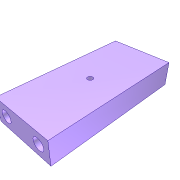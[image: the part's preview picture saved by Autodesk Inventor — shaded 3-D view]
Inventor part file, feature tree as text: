
AUTODESK INVENTOR PART (.ipt)
format: ipt  version: unknown  size: 179,712 bytes
history: native  units: in
note: dims shown in document units (in); Inventor stores cm internally (conversion verified against a paired STEP export)
features: extrude x2, sketch x2
ambient origin geometry x8: Origin, YZ Plane, XZ Plane, XY Plane, X Axis, Y Axis, Z Axis, Center Point
feature tree (4):
  extrude  "Extrusion43"  Depth=0.1303in
  extrude  "Extrusion44"  Depth=0.0787in
  sketch  "Sketch43"  dims[d200=0.0787in d201=0.1303in]
  sketch  "Sketch44"  dims[d202=0.1303in d203=0.0787in d204=0.0787in d205=0.0787in d206=0.1575in d207=0.9055in d208=0.0in d209=0.0394in d210=0.3937in d211=0.0in]
